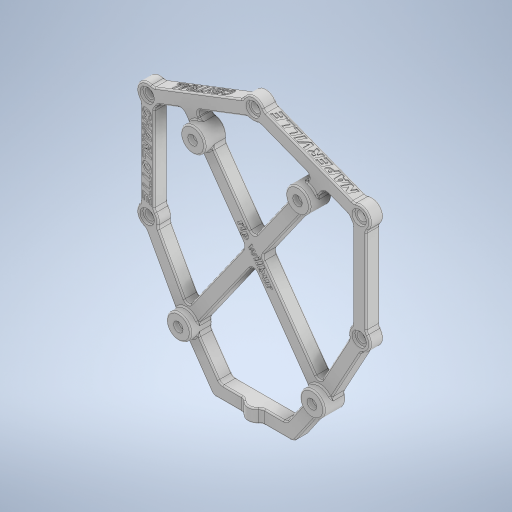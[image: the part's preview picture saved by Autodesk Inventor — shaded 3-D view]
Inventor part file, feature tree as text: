
AUTODESK INVENTOR PART (.ipt)
format: ipt  version: 2024.2 (Build 282272000, 272)  size: 2,063,872 bytes
history: native  units: mm
features: projected_geometry x126, reference x43, sketch x11, extrude x7, other x5, fillet x4, emboss x4, hole x3, plane x1
ambient origin geometry x8: Origin, YZ Plane, XZ Plane, XY Plane, X Axis, Y Axis, Z Axis, Center Point
bodies: Solid1 (feature_tree)
feature tree (204):
  plane  "Work Plane1"
  extrude  "Extrusion1"  Depth=49.0mm
  extrude  "Extrusion4"  Depth=5.25mm
  sketch  "Sketch2"  dims[d2=62.0mm d3=5.25mm]
  extrude  "Extrusion2"  Depth=18.0mm
  extrude  "Extrusion3"  Depth=2.5mm
  hole  "Hole1"  [1 undecoded]
  hole  "Hole2"  [1 undecoded]
  sketch  "Sketch6"  dims[d10=2.5mm d11=2.5mm]
  extrude  "Extrusion5"  Depth=5.000004mm
  hole  "Hole3"  [1 undecoded]
  fillet  "Fillet1"  Radius=1.9mm
  fillet  "Fillet2"  Radius=6.0mm
  fillet  "Fillet3"  Radius=3.0mm
  fillet  "Fillet4"  Radius=2.0mm
  emboss  "Emboss1"
  emboss  "Emboss2"
  sketch  "Sketch10"  dims[d26=3.5mm d27=6.0mm d28=4.0mm d29=2.0mm d30=90.0deg d31=1.0mm d32=0.0mm]
  emboss  "Emboss4"
  emboss  "Emboss5"
  extrude  "Extrusion6"  Depth=10.0mm
  extrude  "Extrusion7"  Depth=10.0mm TaperAngle=0.0deg
  sketch  "Sketch1"  dims[d0=9.0mm d1=49.0mm]
  reference  "Reference1"
  reference  "Reference2"
  reference  "Reference3"
  reference  "Reference4"
  reference  "Reference5"
  reference  "Reference6"
  reference  "Reference7"
  reference  "Reference8"
  reference  "Reference9"
  reference  "Reference10"
  reference  "Reference11"
  reference  "Reference12"
  reference  "Reference13"
  reference  "Reference14"
  reference  "Reference15"
  reference  "Reference16"
  reference  "Reference17"
  reference  "Reference18"
  reference  "Reference19"
  reference  "Reference20"
  reference  "Reference21"
  reference  "Reference22"
  reference  "Reference23"
  reference  "Reference24"
  reference  "Reference25"
  reference  "Reference26"
  reference  "Reference27"
  reference  "Reference28"
  reference  "Reference29"
  reference  "Reference30"
  reference  "Reference31"
  reference  "Reference32"
  reference  "Reference33"
  reference  "Reference34"
  reference  "Reference35"
  reference  "Reference36"
  reference  "Reference37"
  reference  "Reference38"
  reference  "Reference39"
  reference  "Reference40"
  reference  "Reference41"
  reference  "Reference42"
  reference  "Reference43"
  sketch  "Sketch3"  dims[d4=5.25mm d5=18.0mm]
  sketch  "Sketch4"  dims[d6=5.0mm d7=2.5mm]
  sketch  "Sketch5"  dims[d8=2.5mm d9=5.0mm]
  projected_geometry  "Projected Loop1"
  projected_geometry  "Projected Loop2"
  projected_geometry  "Projected Loop3"
  projected_geometry  "Projected Loop4"
  projected_geometry  "Projected Loop5"
  projected_geometry  "Projected Loop6"
  projected_geometry  "Projected Loop7"
  projected_geometry  "Projected Loop8"
  projected_geometry  "Projected Loop9"
  projected_geometry  "Projected Loop10"
  projected_geometry  "Projected Loop11"
  projected_geometry  "Projected Loop12"
  projected_geometry  "Projected Loop13"
  projected_geometry  "Projected Loop14"
  projected_geometry  "Projected Loop15"
  projected_geometry  "Projected Loop16"
  projected_geometry  "Projected Loop17"
  projected_geometry  "Projected Loop18"
  projected_geometry  "Projected Loop19"
  projected_geometry  "Projected Loop20"
  projected_geometry  "Projected Loop21"
  projected_geometry  "Projected Loop22"
  projected_geometry  "Projected Loop23"
  projected_geometry  "Projected Loop24"
  projected_geometry  "Projected Loop25"
  projected_geometry  "Projected Loop26"
  projected_geometry  "Projected Loop27"
  projected_geometry  "Projected Loop28"
  projected_geometry  "Projected Loop29"
  projected_geometry  "Projected Loop30"
  projected_geometry  "Projected Loop31"
  projected_geometry  "Projected Loop32"
  projected_geometry  "Projected Loop33"
  projected_geometry  "Projected Loop34"
  projected_geometry  "Projected Loop35"
  projected_geometry  "Projected Loop36"
  projected_geometry  "Projected Loop37"
  projected_geometry  "Projected Loop38"
  projected_geometry  "Projected Loop39"
  projected_geometry  "Projected Loop40"
  projected_geometry  "Projected Loop41"
  projected_geometry  "Projected Loop42"
  projected_geometry  "Projected Loop43"
  projected_geometry  "Projected Loop44"
  projected_geometry  "Projected Loop45"
  projected_geometry  "Projected Loop46"
  projected_geometry  "Projected Loop47"
  projected_geometry  "Projected Loop48"
  projected_geometry  "Projected Loop49"
  projected_geometry  "Projected Loop50"
  projected_geometry  "Projected Loop51"
  projected_geometry  "Projected Loop52"
  projected_geometry  "Projected Loop53"
  projected_geometry  "Projected Loop54"
  projected_geometry  "Projected Loop55"
  projected_geometry  "Projected Loop56"
  projected_geometry  "Projected Loop57"
  projected_geometry  "Projected Loop58"
  projected_geometry  "Projected Loop59"
  projected_geometry  "Projected Loop60"
  projected_geometry  "Projected Loop61"
  projected_geometry  "Projected Loop62"
  projected_geometry  "Projected Loop63"
  projected_geometry  "Projected Loop64"
  projected_geometry  "Projected Loop65"
  projected_geometry  "Projected Loop66"
  projected_geometry  "Projected Loop67"
  projected_geometry  "Projected Loop68"
  projected_geometry  "Projected Loop69"
  projected_geometry  "Projected Loop70"
  projected_geometry  "Projected Loop71"
  projected_geometry  "Projected Loop72"
  projected_geometry  "Projected Loop73"
  projected_geometry  "Projected Loop74"
  projected_geometry  "Projected Loop75"
  projected_geometry  "Projected Loop76"
  projected_geometry  "Projected Loop77"
  projected_geometry  "Projected Loop78"
  projected_geometry  "Projected Loop79"
  projected_geometry  "Projected Loop80"
  projected_geometry  "Projected Loop81"
  projected_geometry  "Projected Loop82"
  projected_geometry  "Projected Loop83"
  projected_geometry  "Projected Loop84"
  projected_geometry  "Projected Loop85"
  projected_geometry  "Projected Loop86"
  projected_geometry  "Projected Loop87"
  projected_geometry  "Projected Loop88"
  projected_geometry  "Projected Loop89"
  projected_geometry  "Projected Loop90"
  projected_geometry  "Projected Loop91"
  projected_geometry  "Projected Loop92"
  projected_geometry  "Projected Loop93"
  projected_geometry  "Projected Loop94"
  projected_geometry  "Projected Loop95"
  projected_geometry  "Projected Loop96"
  projected_geometry  "Projected Loop97"
  projected_geometry  "Projected Loop98"
  projected_geometry  "Projected Loop99"
  projected_geometry  "Projected Loop100"
  projected_geometry  "Projected Loop101"
  projected_geometry  "Projected Loop102"
  projected_geometry  "Projected Loop103"
  projected_geometry  "Projected Loop104"
  projected_geometry  "Projected Loop105"
  projected_geometry  "Projected Loop106"
  projected_geometry  "Projected Loop107"
  projected_geometry  "Projected Loop108"
  projected_geometry  "Projected Loop109"
  projected_geometry  "Projected Loop110"
  projected_geometry  "Projected Loop111"
  projected_geometry  "Projected Loop112"
  projected_geometry  "Projected Loop113"
  projected_geometry  "Projected Loop114"
  projected_geometry  "Projected Loop115"
  projected_geometry  "Projected Loop116"
  projected_geometry  "Projected Loop117"
  projected_geometry  "Projected Loop118"
  projected_geometry  "Projected Loop119"
  projected_geometry  "Projected Loop120"
  projected_geometry  "Projected Loop121"
  projected_geometry  "Projected Loop122"
  projected_geometry  "Projected Loop123"
  projected_geometry  "Projected Loop124"
  projected_geometry  "Projected Loop125"
  projected_geometry  "Projected Loop126"
  sketch  "Sketch7"  dims[d14=2.5mm d15=5.000004mm]
  sketch  "Sketch8"  dims[d17=5.6mm d18=5.0mm d19=0.0mm d20=1.9mm d21=0.0mm d22=6.0mm d23=0.0mm d24=3.0mm d25=0.0mm]
  sketch  "Sketch11"  dims[d33=5.25mm d34=6.0mm d35=4.0mm d36=2.0mm d37=90.0deg d38=1.0mm d39=0.0mm d40=2.0mm]
  sketch  "Sketch12"  dims[d41=1.5mm d42=7.0mm d43=3.0mm d44=0.0mm d45=2.8mm d46=6.0mm d47=4.0mm d48=2.0mm d49=90.0deg d50=4.0mm d51=0.0mm d52=0.5mm d53=0.5mm d54=96.0mm d55=5.0mm d56=2.5mm d57=2.5mm d58=5.0mm d60=10.0mm d61=2.5mm d62=2.5mm d63=2.5mm d64=2.5mm d65=2.5mm d66=5.0mm d67=27.0mm d68=0.35mm d69=0.0mm d70=0.35mm d71=0.0mm d74=0.35mm d75=0.0mm d76=0.35mm d77=0.0mm d78=0.2mm d79=0.0mm d80=0.2mm d81=0.0mm]
  other  "<userpath>\Desktop\scioly-robot-tour\Hardware\ipt\v3\v3.iam"
  other  "v3.iam"
  other  "v3chassis:1"
  other  "<userpath>\Desktop\scioly-robot-tour\Hardware\ipt\v3\v2.iam"
  other  "v2.iam"
note: 3 required parameter values undecoded (feature->parameter linkage not recoverable at this tier; creation-order binding heuristic only, values carry confidence <= 0.55)
